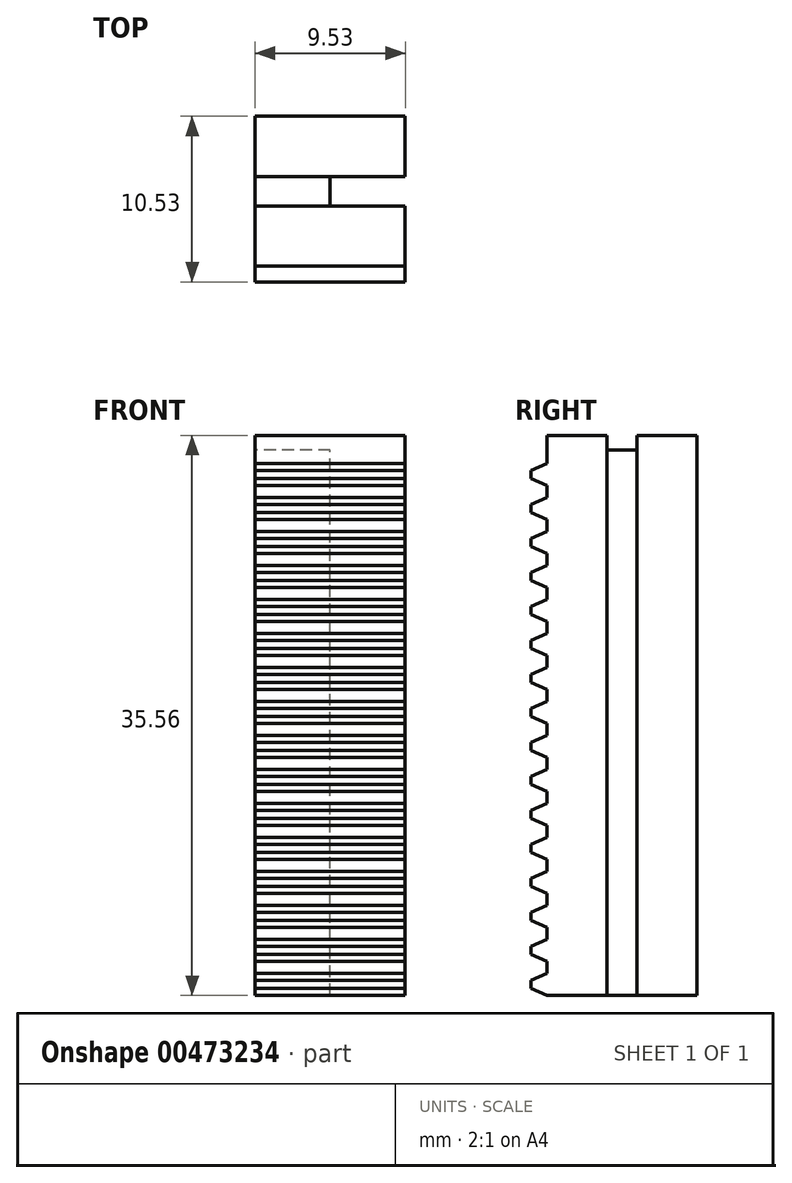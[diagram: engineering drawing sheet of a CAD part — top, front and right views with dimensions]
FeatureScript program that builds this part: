
annotation { "Feature Type Name" : "Feature", "Feature Type Description" : "" }
export const myFeature = defineFeature(function(context is Context, id is Id, definition is map)
    precondition{}
    {
        {
            var Q0;
            Q0=qCreatedBy(makeId("Right.planeOp"),FACE);
            var sketch = newSketch(context, id + "F0", { "sketchPlane" : qUnion([Q0])});
            skLineSegment(sketch, "E0.bottom", {"start": v(0, 0) * mm, "end": v(9.52, 0) * mm});
            skLineSegment(sketch, "E0.top", {"start": v(0, 35.56) * mm, "end": v(3.82, 35.56) * mm});
            skLineSegment(sketch, "E0.left", {"start": v(0, 0) * mm, "end": v(0, 35.56) * mm});
            skLineSegment(sketch, "E0.right", {"start": v(9.52, 0) * mm, "end": v(9.52, 35.56) * mm});
            skLineSegment(sketch, "E1", {"start": v(0, 0) * mm, "end": v(-1, 0.44) * mm});
            skLineSegment(sketch, "E2", {"start": v(-1, 0.44) * mm, "end": v(-1, 0.7) * mm});
            skLineSegment(sketch, "E3.MirrorCS", {"start": v(-1, 0.95) * mm, "end": v(-1, 0.7) * mm});
            skLineSegment(sketch, "E4.MirrorCS", {"start": v(0, 1.38) * mm, "end": v(-1, 0.95) * mm});
            skLineSegment(sketch, "E5.0.1.0", {"start": v(0, 2.16) * mm, "end": v(-1, 2.6) * mm});
            skLineSegment(sketch, "E5.0.1.1", {"start": v(-1, 2.6) * mm, "end": v(-1, 2.85) * mm});
            skLineSegment(sketch, "E5.0.1.2", {"start": v(-1, 3.1) * mm, "end": v(-1, 2.85) * mm});
            skLineSegment(sketch, "E5.0.1.3", {"start": v(0, 3.54) * mm, "end": v(-1, 3.1) * mm});
            skLineSegment(sketch, "E5.0.1.4", {"start": v(0, 2.16) * mm, "end": v(0, 37.72) * mm});
            skLineSegment(sketch, "E5.0.2.0", {"start": v(0, 4.32) * mm, "end": v(-1, 4.75) * mm});
            skLineSegment(sketch, "E5.0.2.1", {"start": v(-1, 4.75) * mm, "end": v(-1, 5) * mm});
            skLineSegment(sketch, "E5.0.2.2", {"start": v(-1, 5.26) * mm, "end": v(-1, 5) * mm});
            skLineSegment(sketch, "E5.0.2.3", {"start": v(0, 5.7) * mm, "end": v(-1, 5.26) * mm});
            skLineSegment(sketch, "E5.0.2.4", {"start": v(0, 4.32) * mm, "end": v(0, 39.88) * mm});
            skLineSegment(sketch, "E5.0.3.0", {"start": v(0, 6.48) * mm, "end": v(-1, 6.91) * mm});
            skLineSegment(sketch, "E5.0.3.1", {"start": v(-1, 6.91) * mm, "end": v(-1, 7.17) * mm});
            skLineSegment(sketch, "E5.0.3.2", {"start": v(-1, 7.42) * mm, "end": v(-1, 7.17) * mm});
            skLineSegment(sketch, "E5.0.3.3", {"start": v(0, 7.86) * mm, "end": v(-1, 7.42) * mm});
            skLineSegment(sketch, "E5.0.3.4", {"start": v(0, 6.48) * mm, "end": v(0, 42.04) * mm});
            skLineSegment(sketch, "E5.0.4.0", {"start": v(0, 8.64) * mm, "end": v(-1, 9.07) * mm});
            skLineSegment(sketch, "E5.0.4.1", {"start": v(-1, 9.07) * mm, "end": v(-1, 9.33) * mm});
            skLineSegment(sketch, "E5.0.4.2", {"start": v(-1, 9.58) * mm, "end": v(-1, 9.33) * mm});
            skLineSegment(sketch, "E5.0.4.3", {"start": v(0, 10.02) * mm, "end": v(-1, 9.58) * mm});
            skLineSegment(sketch, "E5.0.4.4", {"start": v(0, 8.64) * mm, "end": v(0, 44.2) * mm});
            skLineSegment(sketch, "E5.0.5.0", {"start": v(0, 10.8) * mm, "end": v(-1, 11.23) * mm});
            skLineSegment(sketch, "E5.0.5.1", {"start": v(-1, 11.23) * mm, "end": v(-1, 11.49) * mm});
            skLineSegment(sketch, "E5.0.5.2", {"start": v(-1, 11.74) * mm, "end": v(-1, 11.49) * mm});
            skLineSegment(sketch, "E5.0.5.3", {"start": v(0, 12.18) * mm, "end": v(-1, 11.74) * mm});
            skLineSegment(sketch, "E5.0.5.4", {"start": v(0, 10.8) * mm, "end": v(0, 46.35) * mm});
            skLineSegment(sketch, "E5.0.6.0", {"start": v(0, 12.95) * mm, "end": v(-1, 13.39) * mm});
            skLineSegment(sketch, "E5.0.6.1", {"start": v(-1, 13.39) * mm, "end": v(-1, 13.64) * mm});
            skLineSegment(sketch, "E5.0.6.2", {"start": v(-1, 13.9) * mm, "end": v(-1, 13.64) * mm});
            skLineSegment(sketch, "E5.0.6.3", {"start": v(0, 14.34) * mm, "end": v(-1, 13.9) * mm});
            skLineSegment(sketch, "E5.0.6.4", {"start": v(0, 12.95) * mm, "end": v(0, 48.51) * mm});
            skLineSegment(sketch, "E5.0.7.0", {"start": v(0, 15.11) * mm, "end": v(-1, 15.55) * mm});
            skLineSegment(sketch, "E5.0.7.1", {"start": v(-1, 15.55) * mm, "end": v(-1, 15.8) * mm});
            skLineSegment(sketch, "E5.0.7.2", {"start": v(-1, 16.06) * mm, "end": v(-1, 15.8) * mm});
            skLineSegment(sketch, "E5.0.7.3", {"start": v(0, 16.5) * mm, "end": v(-1, 16.06) * mm});
            skLineSegment(sketch, "E5.0.7.4", {"start": v(0, 15.11) * mm, "end": v(0, 50.67) * mm});
            skLineSegment(sketch, "E5.0.8.0", {"start": v(0, 17.27) * mm, "end": v(-1, 17.7) * mm});
            skLineSegment(sketch, "E5.0.8.1", {"start": v(-1, 17.7) * mm, "end": v(-1, 17.96) * mm});
            skLineSegment(sketch, "E5.0.8.2", {"start": v(-1, 18.22) * mm, "end": v(-1, 17.96) * mm});
            skLineSegment(sketch, "E5.0.8.3", {"start": v(0, 18.65) * mm, "end": v(-1, 18.22) * mm});
            skLineSegment(sketch, "E5.0.8.4", {"start": v(0, 17.27) * mm, "end": v(0, 52.83) * mm});
            skLineSegment(sketch, "E5.0.9.0", {"start": v(0, 19.43) * mm, "end": v(-1, 19.87) * mm});
            skLineSegment(sketch, "E5.0.9.1", {"start": v(-1, 19.87) * mm, "end": v(-1, 20.12) * mm});
            skLineSegment(sketch, "E5.0.9.2", {"start": v(-1, 20.38) * mm, "end": v(-1, 20.12) * mm});
            skLineSegment(sketch, "E5.0.9.3", {"start": v(0, 20.81) * mm, "end": v(-1, 20.38) * mm});
            skLineSegment(sketch, "E5.0.9.4", {"start": v(0, 19.43) * mm, "end": v(0, 55) * mm});
            skLineSegment(sketch, "E5.0.10.0", {"start": v(0, 21.59) * mm, "end": v(-1, 22.03) * mm});
            skLineSegment(sketch, "E5.0.10.1", {"start": v(-1, 22.03) * mm, "end": v(-1, 22.28) * mm});
            skLineSegment(sketch, "E5.0.10.2", {"start": v(-1, 22.54) * mm, "end": v(-1, 22.28) * mm});
            skLineSegment(sketch, "E5.0.10.3", {"start": v(0, 22.97) * mm, "end": v(-1, 22.54) * mm});
            skLineSegment(sketch, "E5.0.10.4", {"start": v(0, 21.6) * mm, "end": v(0, 57.15) * mm});
            skLineSegment(sketch, "E5.0.11.0", {"start": v(0, 23.75) * mm, "end": v(-1, 24.18) * mm});
            skLineSegment(sketch, "E5.0.11.1", {"start": v(-1, 24.18) * mm, "end": v(-1, 24.44) * mm});
            skLineSegment(sketch, "E5.0.11.2", {"start": v(-1, 24.7) * mm, "end": v(-1, 24.44) * mm});
            skLineSegment(sketch, "E5.0.11.3", {"start": v(0, 25.13) * mm, "end": v(-1, 24.7) * mm});
            skLineSegment(sketch, "E5.0.11.4", {"start": v(0, 23.75) * mm, "end": v(0, 59.3) * mm});
            skLineSegment(sketch, "E5.0.12.0", {"start": v(0, 25.9) * mm, "end": v(-1, 26.34) * mm});
            skLineSegment(sketch, "E5.0.12.1", {"start": v(-1, 26.34) * mm, "end": v(-1, 26.6) * mm});
            skLineSegment(sketch, "E5.0.12.2", {"start": v(-1, 26.85) * mm, "end": v(-1, 26.6) * mm});
            skLineSegment(sketch, "E5.0.12.3", {"start": v(0, 27.29) * mm, "end": v(-1, 26.85) * mm});
            skLineSegment(sketch, "E5.0.12.4", {"start": v(0, 25.9) * mm, "end": v(0, 61.47) * mm});
            skLineSegment(sketch, "E5.0.13.0", {"start": v(0, 28.07) * mm, "end": v(-1, 28.5) * mm});
            skLineSegment(sketch, "E5.0.13.1", {"start": v(-1, 28.5) * mm, "end": v(-1, 28.76) * mm});
            skLineSegment(sketch, "E5.0.13.2", {"start": v(-1, 29.01) * mm, "end": v(-1, 28.76) * mm});
            skLineSegment(sketch, "E5.0.13.3", {"start": v(0, 29.45) * mm, "end": v(-1, 29.01) * mm});
            skLineSegment(sketch, "E5.0.13.4", {"start": v(0, 28.07) * mm, "end": v(0, 63.63) * mm});
            skLineSegment(sketch, "E5.0.14.0", {"start": v(0, 30.23) * mm, "end": v(-1, 30.66) * mm});
            skLineSegment(sketch, "E5.0.14.1", {"start": v(-1, 30.66) * mm, "end": v(-1, 30.92) * mm});
            skLineSegment(sketch, "E5.0.14.2", {"start": v(-1, 31.17) * mm, "end": v(-1, 30.92) * mm});
            skLineSegment(sketch, "E5.0.14.3", {"start": v(0, 31.6) * mm, "end": v(-1, 31.17) * mm});
            skLineSegment(sketch, "E5.0.14.4", {"start": v(0, 30.23) * mm, "end": v(0, 65.79) * mm});
            skLineSegment(sketch, "E5.direction1", {"start": v(-1, 0.44) * mm, "end": v(24.4, 0.44) * mm, "construction": true});
            skLineSegment(sketch, "E5.direction2", {"start": v(-1, 0.44) * mm, "end": v(-1, 2.6) * mm, "construction": true});
            skLineSegment(sketch, "E6.0.0.15", {"start": v(0, 32.38) * mm, "end": v(-1, 32.82) * mm});
            skLineSegment(sketch, "E6.3.0.15", {"start": v(-1, 32.82) * mm, "end": v(-1, 33.08) * mm});
            skLineSegment(sketch, "E6.6.0.15", {"start": v(-1, 33.33) * mm, "end": v(-1, 33.08) * mm});
            skLineSegment(sketch, "E6.9.0.15", {"start": v(0, 33.77) * mm, "end": v(-1, 33.33) * mm});
            skLineSegment(sketch, "E6.12.0.15", {"start": v(0, 32.39) * mm, "end": v(0, 67.94) * mm});
            skLineSegment(sketch, "E7", {"start": v(3.82, 35.56) * mm, "end": v(3.82, 34.65) * mm});
            skLineSegment(sketch, "E8", {"start": v(3.82, 34.65) * mm, "end": v(4.76, 34.65) * mm});
            skLineSegment(sketch, "E9.MirrorCS", {"start": v(5.7, 34.65) * mm, "end": v(4.76, 34.65) * mm});
            skLineSegment(sketch, "E10.MirrorCS", {"start": v(5.7, 35.56) * mm, "end": v(5.7, 34.65) * mm});
            skLineSegment(sketch, "E11.trimOffspring", {"start": v(5.7, 35.56) * mm, "end": v(9.53, 35.56) * mm});
            skSolve(sketch);
        }
        {
            var Q0;
            Q0=makeQuery(id+"F0.imprint","IMPRINT",FACE,{"disambiguationData":[TD([[makeQuery(id+"F0.imprint","IMPRINT",EDGE,{"derivedFrom":sQuery(id+"F0.wireOp",EDGE,"E0.bottom")}),1.0]])]});
            var Q1;
            {var subQ0=sQuery(id+"F0.wireOp",EDGE,"E1");Q1=makeQuery(id+"F0.imprint","IMPRINT",FACE,{"disambiguationData":[TD([[makeQuery(id+"F0.imprint","IMPRINT",EDGE,{"derivedFrom":subQ0}),-1.0]])]});}
            var Q2;
            {var subQ1=sQuery(id+"F0.wireOp",EDGE,"E5.0.1.0");Q2=makeQuery(id+"F0.imprint","IMPRINT",FACE,{"disambiguationData":[TD([[makeQuery(id+"F0.imprint","IMPRINT",EDGE,{"derivedFrom":subQ1}),-1.0]])]});}
            var Q3;
            {var subQ1=sQuery(id+"F0.wireOp",EDGE,"E5.0.2.0");Q3=makeQuery(id+"F0.imprint","IMPRINT",FACE,{"disambiguationData":[TD([[makeQuery(id+"F0.imprint","IMPRINT",EDGE,{"derivedFrom":subQ1}),-1.0]])]});}
            var Q4;
            {var subQ1=sQuery(id+"F0.wireOp",EDGE,"E5.0.3.0");Q4=makeQuery(id+"F0.imprint","IMPRINT",FACE,{"disambiguationData":[TD([[makeQuery(id+"F0.imprint","IMPRINT",EDGE,{"derivedFrom":subQ1}),-1.0]])]});}
            var Q5;
            {var subQ1=sQuery(id+"F0.wireOp",EDGE,"E5.0.4.0");Q5=makeQuery(id+"F0.imprint","IMPRINT",FACE,{"disambiguationData":[TD([[makeQuery(id+"F0.imprint","IMPRINT",EDGE,{"derivedFrom":subQ1}),-1.0]])]});}
            var Q6;
            {var subQ1=sQuery(id+"F0.wireOp",EDGE,"E5.0.5.0");Q6=makeQuery(id+"F0.imprint","IMPRINT",FACE,{"disambiguationData":[TD([[makeQuery(id+"F0.imprint","IMPRINT",EDGE,{"derivedFrom":subQ1}),-1.0]])]});}
            var Q7;
            {var subQ1=sQuery(id+"F0.wireOp",EDGE,"E5.0.6.0");Q7=makeQuery(id+"F0.imprint","IMPRINT",FACE,{"disambiguationData":[TD([[makeQuery(id+"F0.imprint","IMPRINT",EDGE,{"derivedFrom":subQ1}),-1.0]])]});}
            var Q8;
            {var subQ1=sQuery(id+"F0.wireOp",EDGE,"E5.0.7.0");Q8=makeQuery(id+"F0.imprint","IMPRINT",FACE,{"disambiguationData":[TD([[makeQuery(id+"F0.imprint","IMPRINT",EDGE,{"derivedFrom":subQ1}),-1.0]])]});}
            var Q9;
            {var subQ1=sQuery(id+"F0.wireOp",EDGE,"E5.0.8.0");Q9=makeQuery(id+"F0.imprint","IMPRINT",FACE,{"disambiguationData":[TD([[makeQuery(id+"F0.imprint","IMPRINT",EDGE,{"derivedFrom":subQ1}),-1.0]])]});}
            var Q10;
            {var subQ1=sQuery(id+"F0.wireOp",EDGE,"E5.0.9.0");Q10=makeQuery(id+"F0.imprint","IMPRINT",FACE,{"disambiguationData":[TD([[makeQuery(id+"F0.imprint","IMPRINT",EDGE,{"derivedFrom":subQ1}),-1.0]])]});}
            var Q11;
            {var subQ1=sQuery(id+"F0.wireOp",EDGE,"E5.0.10.0");Q11=makeQuery(id+"F0.imprint","IMPRINT",FACE,{"disambiguationData":[TD([[makeQuery(id+"F0.imprint","IMPRINT",EDGE,{"derivedFrom":subQ1}),-1.0]])]});}
            var Q12;
            {var subQ1=sQuery(id+"F0.wireOp",EDGE,"E5.0.11.0");Q12=makeQuery(id+"F0.imprint","IMPRINT",FACE,{"disambiguationData":[TD([[makeQuery(id+"F0.imprint","IMPRINT",EDGE,{"derivedFrom":subQ1}),-1.0]])]});}
            var Q13;
            {var subQ1=sQuery(id+"F0.wireOp",EDGE,"E5.0.12.0");Q13=makeQuery(id+"F0.imprint","IMPRINT",FACE,{"disambiguationData":[TD([[makeQuery(id+"F0.imprint","IMPRINT",EDGE,{"derivedFrom":subQ1}),-1.0]])]});}
            var Q14;
            {var subQ1=sQuery(id+"F0.wireOp",EDGE,"E5.0.13.0");Q14=makeQuery(id+"F0.imprint","IMPRINT",FACE,{"disambiguationData":[TD([[makeQuery(id+"F0.imprint","IMPRINT",EDGE,{"derivedFrom":subQ1}),-1.0]])]});}
            var Q15;
            {var subQ1=sQuery(id+"F0.wireOp",EDGE,"E5.0.14.0");Q15=makeQuery(id+"F0.imprint","IMPRINT",FACE,{"disambiguationData":[TD([[makeQuery(id+"F0.imprint","IMPRINT",EDGE,{"derivedFrom":subQ1}),-1.0]])]});}
            var Q16;
            {var subQ1=sQuery(id+"F0.wireOp",EDGE,"E6.0.0.15");Q16=makeQuery(id+"F0.imprint","IMPRINT",FACE,{"disambiguationData":[TD([[makeQuery(id+"F0.imprint","IMPRINT",EDGE,{"derivedFrom":subQ1}),-1.0]])]});}
            var Q17;
            {var subQ1=sQuery(id+"F0.wireOp",EDGE,"E6.0.0.16");Q17=makeQuery(id+"F0.imprint","IMPRINT",FACE,{"disambiguationData":[TD([[makeQuery(id+"F0.imprint","IMPRINT",EDGE,{"derivedFrom":subQ1}),-1.0]])]});}
            var Q18;
            {var subQ1=sQuery(id+"F0.wireOp",EDGE,"E6.0.0.17");Q18=makeQuery(id+"F0.imprint","IMPRINT",FACE,{"disambiguationData":[TD([[makeQuery(id+"F0.imprint","IMPRINT",EDGE,{"derivedFrom":subQ1}),-1.0]])]});}
            extrude(context, id + "F1", {"entities" : qUnion([Q0, Q1, Q2, Q3, Q4, Q5, Q6, Q7, Q8, Q9, Q10, Q11, Q12, Q13, Q14, Q15, Q16, Q17, Q18]), "depth" : 9.52 * mm});
        }
        {
            var Q0;
            Q0=makeQuery(id+"F1.opExtrude","SWEPT_FACE",FACE,{"disambiguationData":[OSD([sQuery(id+"F0.wireOp",EDGE,"E8"),sQuery(id+"F0.wireOp",EDGE,"E9.MirrorCS")])]});
            var sketch = newSketch(context, id + "F2", { "sketchPlane" : qUnion([Q0])});
            skLineSegment(sketch, "E12", {"start": v(0, 4.76) * mm, "end": v(9.53, 4.76) * mm});
            skLineSegment(sketch, "E13", {"start": v(4.76, 5.7) * mm, "end": v(4.76, 3.82) * mm});
            skCircle(sketch, "E14", {"center": v(4.76, 4.76) * mm, "radius": 0.8 * mm});
            skSolve(sketch);
        }
        {
            var Q0;
            {var subQ0=sQuery(id+"F2.wireOp",EDGE,"E14");var subQ1=sQuery(id+"F2.wireOp",EDGE,"E12");var subQ2=makeQuery(id+"F2.imprint","INTERSECT",VERTEX,{"disambiguationData":[OD(0.0)],"derivedFrom":[subQ1,subQ0]});Q0=makeQuery(id+"F2.imprint","IMPRINT",FACE,{"disambiguationData":[TD([[makeQuery(id+"F2.imprint","IMPRINT",EDGE,{"disambiguationData":[TD([[subQ2,-1.0]])],"derivedFrom":subQ1}),-1.0]])]});}
            var Q1;
            {var subQ0=sQuery(id+"F2.wireOp",EDGE,"E14");var subQ1=sQuery(id+"F2.wireOp",EDGE,"E12");var subQ2=makeQuery(id+"F2.imprint","INTERSECT",VERTEX,{"disambiguationData":[OD(0.0)],"derivedFrom":[subQ1,subQ0]});Q1=makeQuery(id+"F2.imprint","IMPRINT",FACE,{"disambiguationData":[TD([[makeQuery(id+"F2.imprint","IMPRINT",EDGE,{"disambiguationData":[TD([[subQ2,-1.0]])],"derivedFrom":subQ1}),1.0]])]});}
            var Q2;
            {var subQ0=sQuery(id+"F2.wireOp",EDGE,"E13");var subQ1=sQuery(id+"F2.wireOp",EDGE,"E12");var subQ2=makeQuery(id+"F2.imprint","INTERSECT",VERTEX,{"derivedFrom":[subQ1,subQ0]});Q2=makeQuery(id+"F2.imprint","IMPRINT",FACE,{"disambiguationData":[TD([[makeQuery(id+"F2.imprint","IMPRINT",EDGE,{"disambiguationData":[TD([[subQ2,-1.0]])],"derivedFrom":subQ1}),-1.0]])]});}
            var Q3;
            {var subQ0=sQuery(id+"F2.wireOp",EDGE,"E13");var subQ1=sQuery(id+"F2.wireOp",EDGE,"E12");var subQ2=makeQuery(id+"F2.imprint","INTERSECT",VERTEX,{"derivedFrom":[subQ1,subQ0]});Q3=makeQuery(id+"F2.imprint","IMPRINT",FACE,{"disambiguationData":[TD([[makeQuery(id+"F2.imprint","IMPRINT",EDGE,{"disambiguationData":[TD([[subQ2,-1.0]])],"derivedFrom":subQ1}),1.0]])]});}
            extrude(context, id + "F3", {"entities" : qUnion([Q0, Q1, Q2, Q3]), "operationType" : NewBodyOperationType.REMOVE, "endBound" : BoundingType.UP_TO_NEXT, "oppositeDirection" : true, "depth" : 25.4 * mm});
        }
    });
